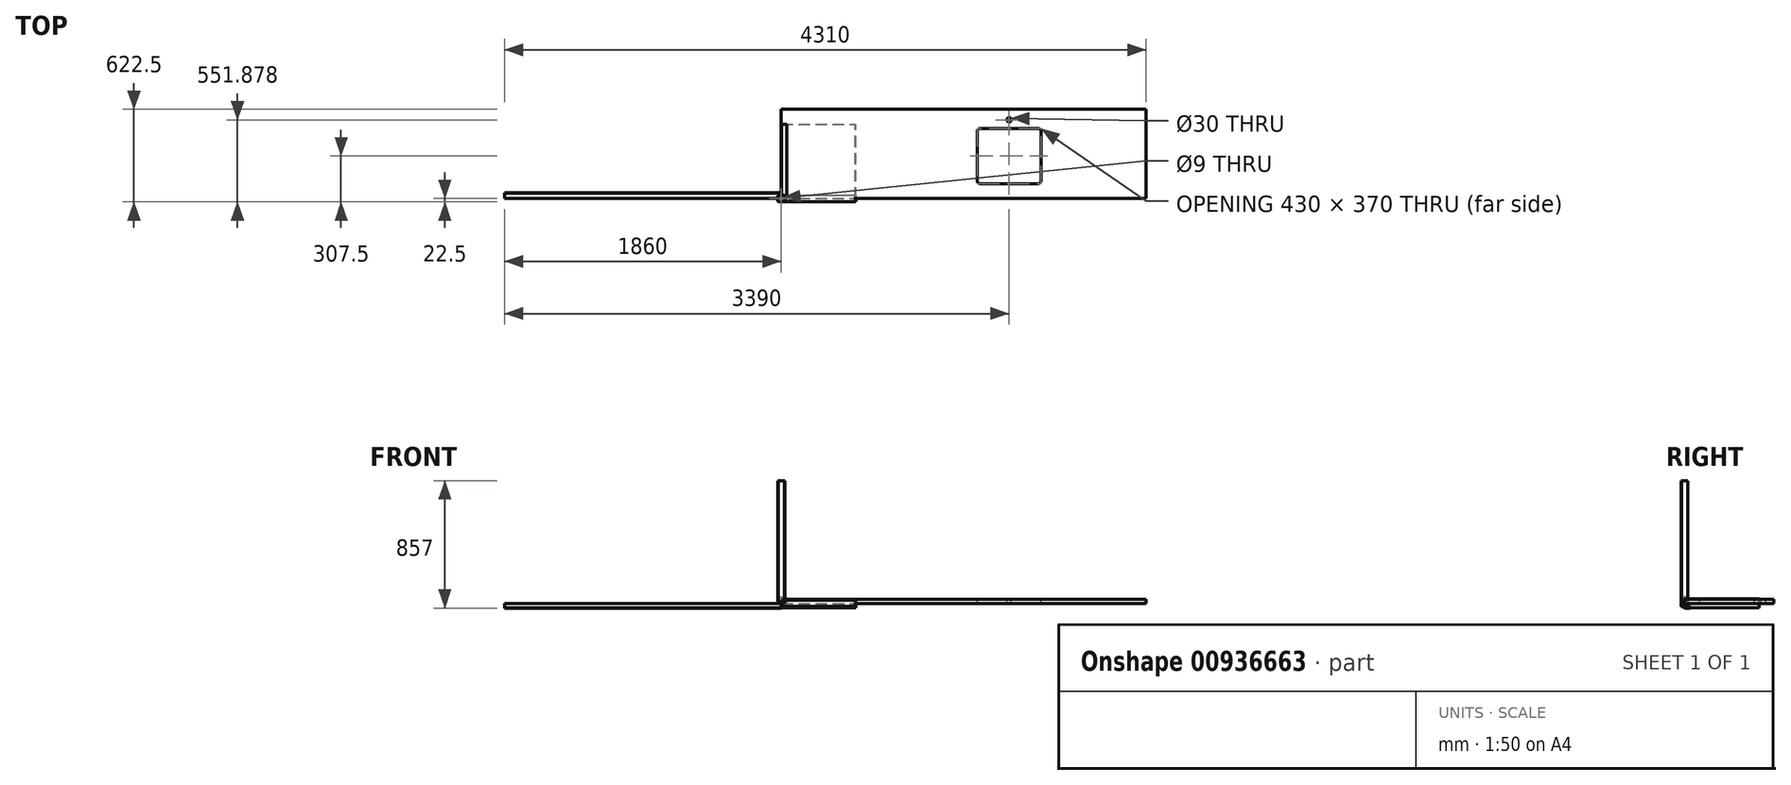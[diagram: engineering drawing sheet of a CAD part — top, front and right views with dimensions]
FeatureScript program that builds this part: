
annotation { "Feature Type Name" : "Feature", "Feature Type Description" : "" }
export const myFeature = defineFeature(function(context is Context, id is Id, definition is map)
    precondition{}
    {
        {
            var Q0;
            Q0=qCreatedBy(makeId("Top.planeOp"),FACE);
            var sketch = newSketch(context, id + "F0", { "sketchPlane" : qUnion([Q0])});
            skLineSegment(sketch, "E0.bottom", {"start": v(22.5, 22.5) * mm, "end": v(-22.5, 22.5) * mm});
            skLineSegment(sketch, "E0.top", {"start": v(22.5, -22.5) * mm, "end": v(-22.5, -22.5) * mm});
            skLineSegment(sketch, "E0.left", {"start": v(22.5, 22.5) * mm, "end": v(22.5, -22.5) * mm});
            skLineSegment(sketch, "E0.right", {"start": v(-22.5, 22.5) * mm, "end": v(-22.5, -22.5) * mm});
            skPoint(sketch, "E0.middle", {"position": v(0, 0) * mm});
            skSolve(sketch);
        }
        {
            var Q0;
            Q0=makeQuery(id+"F0.imprint","IMPRINT",FACE,{"disambiguationData":[TD([[makeQuery(id+"F0.imprint","IMPRINT",EDGE,{"derivedFrom":sQuery(id+"F0.wireOp",EDGE,"E0.bottom")}),1.0]])]});
            extrude(context, id + "F1", {"entities" : qUnion([Q0]), "depth" : 825 * mm, "offsetDistance" : 25 * mm});
        }
        {
            var Q0;
            Q0=qCreatedBy(makeId("Right.planeOp"),FACE);
            var sketch = newSketch(context, id + "F2", { "sketchPlane" : qUnion([Q0])});
            skLineSegment(sketch, "E1.bottom", {"start": v(22.5, 22.5) * mm, "end": v(-22.5, 22.5) * mm});
            skLineSegment(sketch, "E1.top", {"start": v(22.5, -22.5) * mm, "end": v(-22.5, -22.5) * mm});
            skLineSegment(sketch, "E1.left", {"start": v(22.5, 22.5) * mm, "end": v(22.5, -22.5) * mm});
            skLineSegment(sketch, "E1.right", {"start": v(-22.5, 22.5) * mm, "end": v(-22.5, -22.5) * mm});
            skPoint(sketch, "E1.middle", {"position": v(0, 0) * mm});
            skSolve(sketch);
        }
        {
            var Q0;
            Q0=makeQuery(id+"F2.imprint","IMPRINT",FACE,{"disambiguationData":[TD([[makeQuery(id+"F2.imprint","IMPRINT",EDGE,{"derivedFrom":sQuery(id+"F2.wireOp",EDGE,"E1.bottom")}),1.0]])]});
            extrude(context, id + "F3", {"entities" : qUnion([Q0]), "depth" : 500 * mm, "offsetDistance" : 25 * mm});
        }
        {
            var Q0;
            Q0=qCreatedBy(makeId("Top.planeOp"),FACE);
            var sketch = newSketch(context, id + "F4", { "sketchPlane" : qUnion([Q0])});
            skLineSegment(sketch, "E2.bottom", {"start": v(0, 0) * mm, "end": v(2450, 0) * mm});
            skLineSegment(sketch, "E2.top", {"start": v(0, 600) * mm, "end": v(2450, 600) * mm});
            skLineSegment(sketch, "E2.left", {"start": v(0, 0) * mm, "end": v(0, 600) * mm});
            skLineSegment(sketch, "E2.right", {"start": v(2450, 0) * mm, "end": v(2450, 600) * mm});
            skSolve(sketch);
        }
        {
            var Q0;
            Q0=makeQuery(id+"F4.imprint","IMPRINT",FACE,{"disambiguationData":[TD([[makeQuery(id+"F4.imprint","IMPRINT",EDGE,{"derivedFrom":sQuery(id+"F4.wireOp",EDGE,"E2.bottom")}),1.0]])]});
            extrude(context, id + "F5", {"entities" : qUnion([Q0]), "depth" : 27 * mm, "offsetDistance" : 25 * mm});
        }
        {
            var Q0;
            Q0=makeQuery(id+"F5.opExtrude","CAP_EDGE",EDGE,{"disambiguationData":[OSD([sQuery(id+"F4.wireOp",EDGE,"E2.bottom")])],"isStart":false});
            fillet(context, id + "F6", {"entities" : qUnion([Q0]), "radius" : 10 * mm, "tangentPropagation" : true, "allowEdgeOverflow" : false});
        }
        {
            var Q0;
            Q0=makeQuery(id+"F1.opExtrude","SWEPT_EDGE",EDGE,{"disambiguationData":[OSD([sQuery(id+"F0.wireOp",EDGE,"E0.top"),sQuery(id+"F0.wireOp",EDGE,"E0.left")])]});
            var Q1;
            Q1=makeQuery(id+"F1.opExtrude","SWEPT_EDGE",EDGE,{"disambiguationData":[OSD([sQuery(id+"F0.wireOp",EDGE,"E0.bottom"),sQuery(id+"F0.wireOp",EDGE,"E0.left")])]});
            var Q2;
            Q2=makeQuery(id+"F1.opExtrude","SWEPT_EDGE",EDGE,{"disambiguationData":[OSD([sQuery(id+"F0.wireOp",EDGE,"E0.top"),sQuery(id+"F0.wireOp",EDGE,"E0.right")])]});
            var Q3;
            Q3=makeQuery(id+"F1.opExtrude","SWEPT_EDGE",EDGE,{"disambiguationData":[OSD([sQuery(id+"F0.wireOp",EDGE,"E0.bottom"),sQuery(id+"F0.wireOp",EDGE,"E0.right")])]});
            chamfer(context, id + "F7", {"entities" : qUnion([Q0, Q1, Q2, Q3]), "width" : 2 * mm, "tangentPropagation" : true});
        }
        {
            var Q0;
            Q0=makeQuery(id+"F3.opExtrude","SWEPT_EDGE",EDGE,{"disambiguationData":[OSD([sQuery(id+"F2.wireOp",EDGE,"E1.bottom"),sQuery(id+"F2.wireOp",EDGE,"E1.right")])]});
            var Q1;
            Q1=makeQuery(id+"F3.opExtrude","SWEPT_EDGE",EDGE,{"disambiguationData":[OSD([sQuery(id+"F2.wireOp",EDGE,"E1.bottom"),sQuery(id+"F2.wireOp",EDGE,"E1.left")])]});
            var Q2;
            Q2=makeQuery(id+"F3.opExtrude","SWEPT_EDGE",EDGE,{"disambiguationData":[OSD([sQuery(id+"F2.wireOp",EDGE,"E1.top"),sQuery(id+"F2.wireOp",EDGE,"E1.right")])]});
            var Q3;
            Q3=makeQuery(id+"F3.opExtrude","SWEPT_EDGE",EDGE,{"disambiguationData":[OSD([sQuery(id+"F2.wireOp",EDGE,"E1.top"),sQuery(id+"F2.wireOp",EDGE,"E1.left")])]});
            chamfer(context, id + "F8", {"entities" : qUnion([Q0, Q1, Q2, Q3]), "width" : 2 * mm, "tangentPropagation" : true});
        }
        {
            var Q0;
            Q0=makeQuery(id+"F3.opExtrude","CAP_EDGE",EDGE,{"disambiguationData":[OSD([sQuery(id+"F2.wireOp",EDGE,"E1.right")])],"isStart":false});
            var Q1;
            Q1=makeQuery(id+"F3.opExtrude","CAP_EDGE",EDGE,{"disambiguationData":[OSD([sQuery(id+"F2.wireOp",EDGE,"E1.bottom")])],"isStart":false});
            var Q2;
            Q2=makeQuery(id+"F3.opExtrude","CAP_EDGE",EDGE,{"disambiguationData":[OSD([sQuery(id+"F2.wireOp",EDGE,"E1.left")])],"isStart":false});
            var Q3;
            Q3=makeQuery(id+"F3.opExtrude","CAP_EDGE",EDGE,{"disambiguationData":[OSD([sQuery(id+"F2.wireOp",EDGE,"E1.top")])],"isStart":false});
            var Q4;
            Q4=makeQuery(id+"F3.opExtrude","CAP_EDGE",EDGE,{"disambiguationData":[OSD([sQuery(id+"F2.wireOp",EDGE,"E1.bottom")])],"isStart":true});
            var Q5;
            Q5=makeQuery(id+"F3.opExtrude","CAP_EDGE",EDGE,{"disambiguationData":[OSD([sQuery(id+"F2.wireOp",EDGE,"E1.left")])],"isStart":true});
            var Q6;
            Q6=makeQuery(id+"F3.opExtrude","CAP_EDGE",EDGE,{"disambiguationData":[OSD([sQuery(id+"F2.wireOp",EDGE,"E1.top")])],"isStart":true});
            var Q7;
            Q7=makeQuery(id+"F3.opExtrude","CAP_EDGE",EDGE,{"disambiguationData":[OSD([sQuery(id+"F2.wireOp",EDGE,"E1.right")])],"isStart":true});
            chamfer(context, id + "F9", {"entities" : qUnion([Q0, Q1, Q2, Q3, Q4, Q5, Q6, Q7]), "width" : 2 * mm, "tangentPropagation" : true});
        }
        {
            var Q0;
            Q0=qCreatedBy(makeId("Front.planeOp"),FACE);
            var sketch = newSketch(context, id + "F10", { "sketchPlane" : qUnion([Q0])});
            skLineSegment(sketch, "E3.bottom", {"start": v(0, 0) * mm, "end": v(38, 0) * mm});
            skLineSegment(sketch, "E3.top", {"start": v(0, 32) * mm, "end": v(38, 32) * mm});
            skLineSegment(sketch, "E3.left", {"start": v(0, 0) * mm, "end": v(0, 32) * mm});
            skLineSegment(sketch, "E3.right", {"start": v(38, 0) * mm, "end": v(38, 32) * mm});
            skSolve(sketch);
        }
        {
            var Q0;
            Q0=makeQuery(id+"F10.imprint","IMPRINT",FACE,{"disambiguationData":[TD([[makeQuery(id+"F10.imprint","IMPRINT",EDGE,{"derivedFrom":sQuery(id+"F10.wireOp",EDGE,"E3.bottom")}),1.0]])]});
            extrude(context, id + "F11", {"entities" : qUnion([Q0]), "oppositeDirection" : true, "depth" : 500 * mm, "offsetDistance" : 25 * mm});
        }
        {
            var Q0;
            Q0=makeQuery(id+"F11.opExtrude","SWEPT_EDGE",EDGE,{"disambiguationData":[OSD([sQuery(id+"F10.wireOp",EDGE,"E3.top"),sQuery(id+"F10.wireOp",EDGE,"E3.left")])]});
            var Q1;
            Q1=makeQuery(id+"F11.opExtrude","SWEPT_EDGE",EDGE,{"disambiguationData":[OSD([sQuery(id+"F10.wireOp",EDGE,"E3.top"),sQuery(id+"F10.wireOp",EDGE,"E3.right")])]});
            var Q2;
            Q2=makeQuery(id+"F11.opExtrude","SWEPT_EDGE",EDGE,{"disambiguationData":[OSD([sQuery(id+"F10.wireOp",EDGE,"E3.bottom"),sQuery(id+"F10.wireOp",EDGE,"E3.left")])]});
            var Q3;
            Q3=makeQuery(id+"F11.opExtrude","SWEPT_EDGE",EDGE,{"disambiguationData":[OSD([sQuery(id+"F10.wireOp",EDGE,"E3.bottom"),sQuery(id+"F10.wireOp",EDGE,"E3.right")])]});
            chamfer(context, id + "F12", {"entities" : qUnion([Q0, Q1, Q2, Q3]), "width" : 2 * mm, "tangentPropagation" : true});
        }
        {
            var Q0;
            Q0=makeQuery(id+"F1.opExtrude","CAP_FACE",FACE,{"disambiguationData":[OSD([sQuery(id+"F0.wireOp",EDGE,"E0.bottom"),sQuery(id+"F0.wireOp",EDGE,"E0.top"),sQuery(id+"F0.wireOp",EDGE,"E0.left"),sQuery(id+"F0.wireOp",EDGE,"E0.right")])],"isStart":true});
            var sketch = newSketch(context, id + "F13", { "sketchPlane" : qUnion([Q0])});
            skPoint(sketch, "E4", {"position": v(0, 0) * mm});
            skSolve(sketch);
        }
        {
            var Q0;
            Q0=sQuery(id+"F13.wireOp",VERTEX,"E4");
            var Q1;
            Q1=makeQuery(id+"F1.opExtrude","SWEPT_BODY",BODY,{"disambiguationData":[OSD([sQuery(id+"F0.wireOp",EDGE,"E0.bottom"),sQuery(id+"F0.wireOp",EDGE,"E0.top"),sQuery(id+"F0.wireOp",EDGE,"E0.left"),sQuery(id+"F0.wireOp",EDGE,"E0.right")])]});
            hole(context, id + "F14", {"style" : HoleStyle.SIMPLE, "endStyle" : HoleEndStyle.BLIND, "holeDiameter" : 9 * mm, "majorDiameter" : 5 * mm, "holeDepth" : 30 * mm, "isTappedThrough" : true, "tappedDepth" : 12 * mm, "tapClearance" : 3, "locations" : qUnion([Q0]), "scope" : qUnion([Q1])});
        }
        {
            var Q0;
            Q0=qCreatedBy(makeId("Front.planeOp"),FACE);
            var sketch = newSketch(context, id + "F15", { "sketchPlane" : qUnion([Q0])});
            skLineSegment(sketch, "E5", {"start": v(0, 0) * mm, "end": v(0, 45) * mm, "construction": true});
            skLineSegment(sketch, "E6", {"start": v(0, 45) * mm, "end": v(4, 45) * mm});
            skLineSegment(sketch, "E7", {"start": v(4, 45) * mm, "end": v(4, 10) * mm});
            skLineSegment(sketch, "E8", {"start": v(4, 10) * mm, "end": v(20, 3.4) * mm});
            skLineSegment(sketch, "E9", {"start": v(20, 3.4) * mm, "end": v(20, 0) * mm});
            skLineSegment(sketch, "E10", {"start": v(20, 0) * mm, "end": v(0, 0) * mm});
            skLineSegment(sketch, "E11", {"start": v(0, 45) * mm, "end": v(0, 0) * mm});
            skSolve(sketch);
        }
        {
            var Q0;
            Q0=makeQuery(id+"F15.imprint","IMPRINT",FACE,{"disambiguationData":[TD([[makeQuery(id+"F15.imprint","IMPRINT",EDGE,{"derivedFrom":sQuery(id+"F15.wireOp",EDGE,"E6")}),-1.0]])]});
            var Q1;
            Q1=sQuery(id+"F15.wireOp",EDGE,"E5");
            revolve(context, id + "F16", {"surfaceOperationType" : NewSurfaceOperationType.NEW, "entities" : qUnion([Q0]), "axis" : qUnion([Q1]), "revolveType" : RevolveType.FULL});
        }
        {
            var Q0;
            Q0=makeQuery(id+"F5.opExtrude","CAP_FACE",FACE,{"disambiguationData":[OSD([sQuery(id+"F4.wireOp",EDGE,"E2.bottom"),sQuery(id+"F4.wireOp",EDGE,"E2.top"),sQuery(id+"F4.wireOp",EDGE,"E2.left"),sQuery(id+"F4.wireOp",EDGE,"E2.right")])],"isStart":false});
            var sketch = newSketch(context, id + "F17", { "sketchPlane" : qUnion([Q0])});
            skLineSegment(sketch, "E12.bottom", {"start": v(1335, 470) * mm, "end": v(1725, 470) * mm});
            skLineSegment(sketch, "E12.top", {"start": v(1335, 100) * mm, "end": v(1725, 100) * mm});
            skLineSegment(sketch, "E12.left", {"start": v(1315, 450) * mm, "end": v(1315, 120) * mm});
            skLineSegment(sketch, "E12.right", {"start": v(1745, 450) * mm, "end": v(1745, 120) * mm});
            skPoint(sketch, "E13.visualSharp", {"position": v(1315, 470) * mm});
            skArc(sketch, "E13.filletArc", {"start": v(1335, 470) * mm, "mid": v(1320.86, 464.14) * mm, "end": v(1315, 450) * mm});
            skPoint(sketch, "E14.visualSharp", {"position": v(1745, 470) * mm});
            skArc(sketch, "E14.filletArc", {"start": v(1745, 450) * mm, "mid": v(1739.14, 464.14) * mm, "end": v(1725, 470) * mm});
            skPoint(sketch, "E15.visualSharp", {"position": v(1745, 100) * mm});
            skArc(sketch, "E15.filletArc", {"start": v(1725, 100) * mm, "mid": v(1739.14, 105.86) * mm, "end": v(1745, 120) * mm});
            skPoint(sketch, "E16.visualSharp", {"position": v(1315, 100) * mm});
            skArc(sketch, "E16.filletArc", {"start": v(1315, 120) * mm, "mid": v(1320.86, 105.86) * mm, "end": v(1335, 100) * mm});
            skSolve(sketch);
        }
        {
            var Q0;
            Q0=makeQuery(id+"F17.imprint","IMPRINT",FACE,{"disambiguationData":[TD([[makeQuery(id+"F17.imprint","IMPRINT",EDGE,{"derivedFrom":sQuery(id+"F17.wireOp",EDGE,"E12.bottom")}),-1.0]])]});
            extrude(context, id + "F18", {"entities" : qUnion([Q0]), "operationType" : NewBodyOperationType.REMOVE, "endBound" : BoundingType.THROUGH_ALL, "oppositeDirection" : true, "depth" : 25 * mm, "offsetDistance" : 25 * mm});
        }
        {
            var Q0;
            Q0=makeQuery(id+"F5.opExtrude","CAP_FACE",FACE,{"disambiguationData":[OSD([sQuery(id+"F4.wireOp",EDGE,"E2.bottom"),sQuery(id+"F4.wireOp",EDGE,"E2.top"),sQuery(id+"F4.wireOp",EDGE,"E2.left"),sQuery(id+"F4.wireOp",EDGE,"E2.right")])],"isStart":false});
            var sketch = newSketch(context, id + "F19", { "sketchPlane" : qUnion([Q0])});
            skPoint(sketch, "E17", {"position": v(1530, 529.38) * mm});
            skSolve(sketch);
        }
        {
            var Q0;
            Q0=sQuery(id+"F19.wireOp",VERTEX,"E17");
            var Q1;
            Q1=makeQuery(id+"F5.opExtrude","SWEPT_BODY",BODY,{"disambiguationData":[OSD([sQuery(id+"F4.wireOp",EDGE,"E2.bottom"),sQuery(id+"F4.wireOp",EDGE,"E2.top"),sQuery(id+"F4.wireOp",EDGE,"E2.left"),sQuery(id+"F4.wireOp",EDGE,"E2.right")])]});
            hole(context, id + "F20", {"style" : HoleStyle.SIMPLE, "endStyle" : HoleEndStyle.THROUGH, "holeDiameter" : 30 * mm, "majorDiameter" : 5 * mm, "isTappedThrough" : true, "tappedDepth" : 12 * mm, "tapClearance" : 3, "locations" : qUnion([Q0]), "scope" : qUnion([Q1])});
        }
        {
            var Q0;
            Q0=qCreatedBy(makeId("Right.planeOp"),FACE);
            var sketch = newSketch(context, id + "F21", { "sketchPlane" : qUnion([Q0])});
            skLineSegment(sketch, "E18.bottom", {"start": v(0, 0) * mm, "end": v(38, 0) * mm});
            skLineSegment(sketch, "E18.top", {"start": v(0, -32) * mm, "end": v(38, -32) * mm});
            skLineSegment(sketch, "E18.left", {"start": v(0, 0) * mm, "end": v(0, -32) * mm});
            skLineSegment(sketch, "E18.right", {"start": v(38, 0) * mm, "end": v(38, -32) * mm});
            skSolve(sketch);
        }
        {
            var Q0;
            Q0=makeQuery(id+"F21.imprint","IMPRINT",FACE,{"disambiguationData":[TD([[makeQuery(id+"F21.imprint","IMPRINT",EDGE,{"derivedFrom":sQuery(id+"F21.wireOp",EDGE,"E18.bottom")}),-1.0]])]});
            extrude(context, id + "F22", {"entities" : qUnion([Q0]), "oppositeDirection" : true, "depth" : 1860 * mm, "offsetDistance" : 25 * mm});
        }
        {
            var Q0;
            Q0=makeQuery(id+"F22.opExtrude","SWEPT_EDGE",EDGE,{"disambiguationData":[OSD([sQuery(id+"F21.wireOp",EDGE,"E18.bottom"),sQuery(id+"F21.wireOp",EDGE,"E18.left")])]});
            var Q1;
            Q1=makeQuery(id+"F22.opExtrude","SWEPT_EDGE",EDGE,{"disambiguationData":[OSD([sQuery(id+"F21.wireOp",EDGE,"E18.bottom"),sQuery(id+"F21.wireOp",EDGE,"E18.right")])]});
            var Q2;
            Q2=makeQuery(id+"F22.opExtrude","CAP_EDGE",EDGE,{"disambiguationData":[OSD([sQuery(id+"F21.wireOp",EDGE,"E18.right")])],"isStart":true});
            var Q3;
            Q3=makeQuery(id+"F22.opExtrude","CAP_EDGE",EDGE,{"disambiguationData":[OSD([sQuery(id+"F21.wireOp",EDGE,"E18.top")])],"isStart":true});
            var Q4;
            Q4=makeQuery(id+"F22.opExtrude","CAP_EDGE",EDGE,{"disambiguationData":[OSD([sQuery(id+"F21.wireOp",EDGE,"E18.bottom")])],"isStart":true});
            var Q5;
            Q5=makeQuery(id+"F22.opExtrude","CAP_EDGE",EDGE,{"disambiguationData":[OSD([sQuery(id+"F21.wireOp",EDGE,"E18.left")])],"isStart":true});
            var Q6;
            Q6=makeQuery(id+"F22.opExtrude","SWEPT_EDGE",EDGE,{"disambiguationData":[OSD([sQuery(id+"F21.wireOp",EDGE,"E18.top"),sQuery(id+"F21.wireOp",EDGE,"E18.left")])]});
            var Q7;
            Q7=makeQuery(id+"F22.opExtrude","SWEPT_EDGE",EDGE,{"disambiguationData":[OSD([sQuery(id+"F21.wireOp",EDGE,"E18.top"),sQuery(id+"F21.wireOp",EDGE,"E18.right")])]});
            var Q8;
            Q8=makeQuery(id+"F22.opExtrude","CAP_EDGE",EDGE,{"disambiguationData":[OSD([sQuery(id+"F21.wireOp",EDGE,"E18.left")])],"isStart":false});
            var Q9;
            Q9=makeQuery(id+"F22.opExtrude","CAP_EDGE",EDGE,{"disambiguationData":[OSD([sQuery(id+"F21.wireOp",EDGE,"E18.top")])],"isStart":false});
            var Q10;
            Q10=makeQuery(id+"F22.opExtrude","CAP_EDGE",EDGE,{"disambiguationData":[OSD([sQuery(id+"F21.wireOp",EDGE,"E18.bottom")])],"isStart":false});
            var Q11;
            Q11=makeQuery(id+"F22.opExtrude","CAP_EDGE",EDGE,{"disambiguationData":[OSD([sQuery(id+"F21.wireOp",EDGE,"E18.right")])],"isStart":false});
            chamfer(context, id + "F23", {"entities" : qUnion([Q0, Q1, Q2, Q3, Q4, Q5, Q6, Q7, Q8, Q9, Q10, Q11]), "width" : 2 * mm, "tangentPropagation" : true});
        }
        {
            var Q0;
            Q0=qCreatedBy(makeId("Top.planeOp"),FACE);
            var sketch = newSketch(context, id + "F24", { "sketchPlane" : qUnion([Q0])});
            skLineSegment(sketch, "E19.bottom", {"start": v(0, 0) * mm, "end": v(500, 0) * mm});
            skLineSegment(sketch, "E19.top", {"start": v(0, 500) * mm, "end": v(500, 500) * mm});
            skLineSegment(sketch, "E19.left", {"start": v(0, 0) * mm, "end": v(0, 500) * mm});
            skLineSegment(sketch, "E19.right", {"start": v(500, 0) * mm, "end": v(500, 500) * mm});
            skSolve(sketch);
        }
        {
            var Q0;
            Q0=makeQuery(id+"F24.imprint","IMPRINT",FACE,{"disambiguationData":[TD([[makeQuery(id+"F24.imprint","IMPRINT",EDGE,{"derivedFrom":sQuery(id+"F24.wireOp",EDGE,"E19.bottom")}),1.0]])]});
            extrude(context, id + "F25", {"entities" : qUnion([Q0]), "depth" : -30 * mm, "offsetDistance" : 25 * mm});
        }
        {
            var Q0;
            Q0=makeQuery(id+"F25.opExtrude","CAP_EDGE",EDGE,{"disambiguationData":[OSD([sQuery(id+"F24.wireOp",EDGE,"E19.bottom")])],"isStart":true});
            var Q1;
            Q1=makeQuery(id+"F25.opExtrude","CAP_EDGE",EDGE,{"disambiguationData":[OSD([sQuery(id+"F24.wireOp",EDGE,"E19.right")])],"isStart":true});
            var Q2;
            Q2=makeQuery(id+"F25.opExtrude","CAP_EDGE",EDGE,{"disambiguationData":[OSD([sQuery(id+"F24.wireOp",EDGE,"E19.top")])],"isStart":true});
            var Q3;
            Q3=makeQuery(id+"F25.opExtrude","CAP_EDGE",EDGE,{"disambiguationData":[OSD([sQuery(id+"F24.wireOp",EDGE,"E19.left")])],"isStart":true});
            fillet(context, id + "F26", {"entities" : qUnion([Q0, Q1, Q2, Q3]), "radius" : 3 * mm, "tangentPropagation" : true, "allowEdgeOverflow" : false});
        }
        {
            var Q0;
            Q0=makeQuery(id+"F25.opExtrude","CAP_FACE",FACE,{"disambiguationData":[OSD([sQuery(id+"F24.wireOp",EDGE,"E19.bottom"),sQuery(id+"F24.wireOp",EDGE,"E19.top"),sQuery(id+"F24.wireOp",EDGE,"E19.left"),sQuery(id+"F24.wireOp",EDGE,"E19.right")])],"isStart":false});
            shell(context, id + "F27", {"entities" : qUnion([Q0]), "thickness" : 1.5 * mm});
        }
    });
